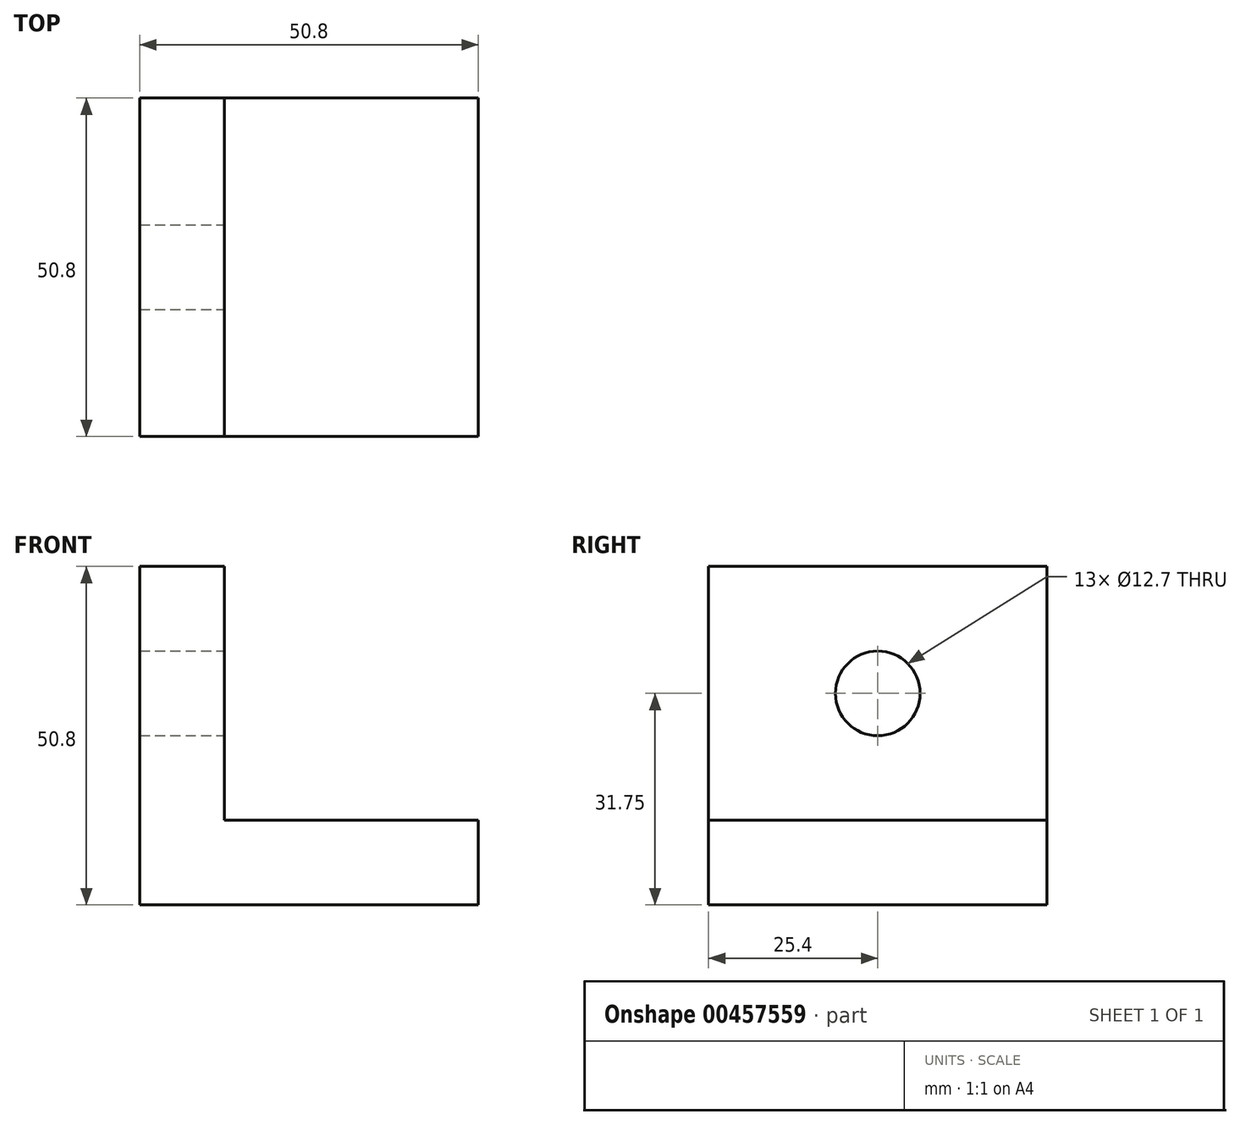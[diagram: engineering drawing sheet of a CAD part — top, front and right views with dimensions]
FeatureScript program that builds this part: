
annotation { "Feature Type Name" : "Feature", "Feature Type Description" : "" }
export const myFeature = defineFeature(function(context is Context, id is Id, definition is map)
    precondition{}
    {
        {
            var Q0;
            Q0=qCreatedBy(makeId("Front.planeOp"),FACE);
            var sketch = newSketch(context, id + "F0", { "sketchPlane" : qUnion([Q0])});
            skLineSegment(sketch, "E0", {"start": v(-50.27, 49.07) * mm, "end": v(-50.27, -1.73) * mm});
            skLineSegment(sketch, "E1", {"start": v(-50.27, -1.73) * mm, "end": v(0.53, -1.73) * mm});
            skLineSegment(sketch, "E2", {"start": v(0.53, -1.73) * mm, "end": v(0.53, 10.97) * mm});
            skLineSegment(sketch, "E3", {"start": v(0.53, 10.97) * mm, "end": v(-37.57, 10.97) * mm});
            skLineSegment(sketch, "E4", {"start": v(-37.57, 49.07) * mm, "end": v(-37.57, 10.97) * mm});
            skLineSegment(sketch, "E5", {"start": v(-50.27, 49.07) * mm, "end": v(-37.57, 49.07) * mm});
            skSolve(sketch);
        }
        {
            var Q0;
            Q0 = qSketchRegion(id + "F0", true);
            extrude(context, id + "F1", {"entities" : qUnion([Q0]), "oppositeDirection" : true, "depth" : 50.8 * mm});
        }
        {
            var Q0;
            Q0=makeQuery(id+"F1.opExtrude","SWEPT_FACE",FACE,{"disambiguationData":[OSD([sQuery(id+"F0.wireOp",EDGE,"E4")])]});
            var sketch = newSketch(context, id + "F2", { "sketchPlane" : qUnion([Q0])});
            skLineSegment(sketch, "E6", {"start": v(34, 30.02) * mm, "end": v(0, 30.02) * mm, "construction": true});
            skPoint(sketch, "E6.startSnap0", {"position": v(0, 30.02) * mm});
            skLineSegment(sketch, "E7", {"start": v(25.4, 49.07) * mm, "end": v(25.4, 30.02) * mm, "construction": true});
            skCircle(sketch, "E8", {"center": v(25.4, 30.02) * mm, "radius": 6.35 * mm});
            skSolve(sketch);
        }
        {
            var Q0;
            Q0=makeQuery(id+"F2.imprint","IMPRINT",FACE,{"disambiguationData":[TD([[makeQuery(id+"F2.imprint","IMPRINT",EDGE,{"derivedFrom":sQuery(id+"F2.wireOp",EDGE,"E8")}),1.0]])]});
            extrude(context, id + "F3", {"entities" : qUnion([Q0]), "operationType" : NewBodyOperationType.REMOVE, "oppositeDirection" : true, "depth" : 12.7 * mm});
        }
    });
